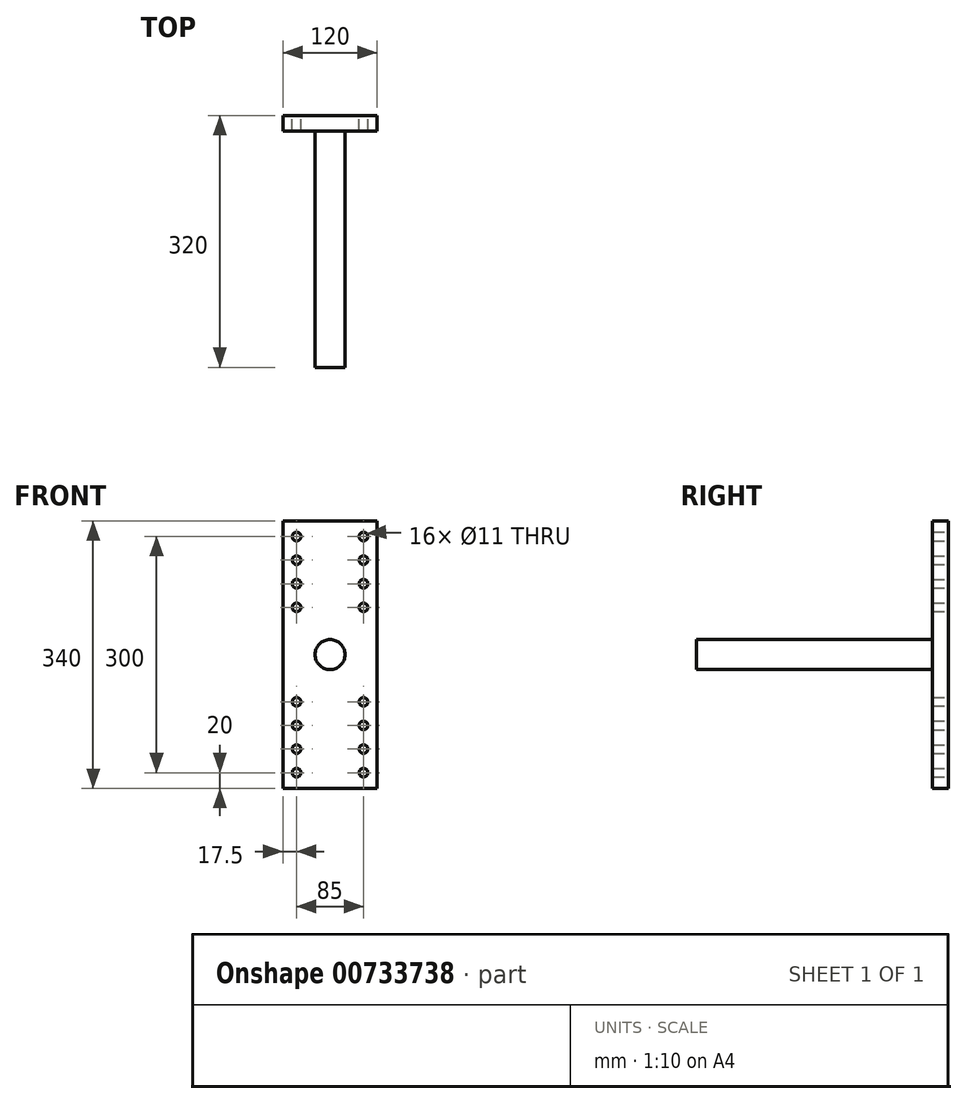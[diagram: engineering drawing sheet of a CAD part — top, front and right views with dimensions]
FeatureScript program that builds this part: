
annotation { "Feature Type Name" : "Feature", "Feature Type Description" : "" }
export const myFeature = defineFeature(function(context is Context, id is Id, definition is map)
    precondition{}
    {
        {
            var Q0;
            Q0=qCreatedBy(makeId("Front.planeOp"),FACE);
            var sketch = newSketch(context, id + "F0", { "sketchPlane" : qUnion([Q0])});
            skLineSegment(sketch, "E0.bottom", {"start": v(60, -170) * mm, "end": v(-60, -170) * mm});
            skLineSegment(sketch, "E0.top", {"start": v(60, 170) * mm, "end": v(-60, 170) * mm});
            skLineSegment(sketch, "E0.left", {"start": v(60, -170) * mm, "end": v(60, 170) * mm});
            skLineSegment(sketch, "E0.right", {"start": v(-60, -170) * mm, "end": v(-60, 170) * mm});
            skPoint(sketch, "E0.middle", {"position": v(0, 0) * mm});
            skLineSegment(sketch, "E1", {"start": v(0, 0) * mm, "end": v(42.5, 0) * mm, "construction": true});
            skPoint(sketch, "E1.endSnap0", {"position": v(60, 0) * mm});
            skCircle(sketch, "E2", {"center": v(42.5, 270) * mm, "radius": 5.5 * mm});
            skCircle(sketch, "E3.0.1.0", {"center": v(42.5, 240) * mm, "radius": 5.5 * mm});
            skCircle(sketch, "E3.0.2.0", {"center": v(42.5, 210) * mm, "radius": 5.5 * mm});
            skCircle(sketch, "E3.0.3.0", {"center": v(42.5, 180) * mm, "radius": 5.5 * mm});
            skCircle(sketch, "E3.0.4.0", {"center": v(42.5, 150) * mm, "radius": 5.5 * mm});
            skCircle(sketch, "E3.0.5.0", {"center": v(42.5, 120) * mm, "radius": 5.5 * mm});
            skLineSegment(sketch, "E3.direction1", {"start": v(42.5, 270) * mm, "end": v(67.5, 270) * mm, "construction": true});
            skLineSegment(sketch, "E3.direction2", {"start": v(42.5, 270) * mm, "end": v(42.5, 240) * mm, "construction": true});
            skCircle(sketch, "E4.0.0.6", {"center": v(42.5, 90) * mm, "radius": 5.5 * mm});
            skCircle(sketch, "E4.0.0.7", {"center": v(42.5, 60) * mm, "radius": 5.5 * mm});
            skCircle(sketch, "E5.MirrorC", {"center": v(42.5, -150) * mm, "radius": 5.5 * mm});
            skCircle(sketch, "E6.MirrorC", {"center": v(42.5, -270) * mm, "radius": 5.5 * mm});
            skCircle(sketch, "E7.MirrorC", {"center": v(42.5, -240) * mm, "radius": 5.5 * mm});
            skCircle(sketch, "E8.MirrorC", {"center": v(42.5, -210) * mm, "radius": 5.5 * mm});
            skCircle(sketch, "E9.MirrorC", {"center": v(42.5, -180) * mm, "radius": 5.5 * mm});
            skCircle(sketch, "E10.MirrorC", {"center": v(42.5, -120) * mm, "radius": 5.5 * mm});
            skCircle(sketch, "E11.MirrorC", {"center": v(42.5, -90) * mm, "radius": 5.5 * mm});
            skLineSegment(sketch, "E12.MirrorCS", {"start": v(42.5, -270) * mm, "end": v(42.5, -240) * mm, "construction": true});
            skCircle(sketch, "E13.MirrorC", {"center": v(42.5, -60) * mm, "radius": 5.5 * mm});
            skLineSegment(sketch, "E14.MirrorCS", {"start": v(42.5, -270) * mm, "end": v(67.5, -270) * mm, "construction": true});
            skLineSegment(sketch, "E15", {"start": v(0, 0) * mm, "end": v(0, 50) * mm, "construction": true});
            skCircle(sketch, "E16.MirrorC", {"center": v(-42.5, -240) * mm, "radius": 5.5 * mm});
            skCircle(sketch, "E17.MirrorC", {"center": v(-42.5, 90) * mm, "radius": 5.5 * mm});
            skLineSegment(sketch, "E18.MirrorCS", {"start": v(-42.5, 270) * mm, "end": v(-42.5, 240) * mm, "construction": true});
            skCircle(sketch, "E19.MirrorC", {"center": v(-42.5, 120) * mm, "radius": 5.5 * mm});
            skCircle(sketch, "E20.MirrorC", {"center": v(-42.5, -210) * mm, "radius": 5.5 * mm});
            skCircle(sketch, "E21.MirrorC", {"center": v(-42.5, 150) * mm, "radius": 5.5 * mm});
            skCircle(sketch, "E22.MirrorC", {"center": v(-42.5, -150) * mm, "radius": 5.5 * mm});
            skCircle(sketch, "E23.MirrorC", {"center": v(-42.5, 210) * mm, "radius": 5.5 * mm});
            skCircle(sketch, "E24.MirrorC", {"center": v(-42.5, 60) * mm, "radius": 5.5 * mm});
            skCircle(sketch, "E25.MirrorC", {"center": v(-42.5, -180) * mm, "radius": 5.5 * mm});
            skCircle(sketch, "E26.MirrorC", {"center": v(-42.5, -120) * mm, "radius": 5.5 * mm});
            skLineSegment(sketch, "E27.MirrorCS", {"start": v(-42.5, -270) * mm, "end": v(-42.5, -240) * mm, "construction": true});
            skCircle(sketch, "E28.MirrorC", {"center": v(-42.5, 180) * mm, "radius": 5.5 * mm});
            skCircle(sketch, "E29.MirrorC", {"center": v(-42.5, 240) * mm, "radius": 5.5 * mm});
            skCircle(sketch, "E30.MirrorC", {"center": v(-42.5, -270) * mm, "radius": 5.5 * mm});
            skCircle(sketch, "E31.MirrorC", {"center": v(-42.5, -60) * mm, "radius": 5.5 * mm});
            skCircle(sketch, "E32.MirrorC", {"center": v(-42.5, 270) * mm, "radius": 5.5 * mm});
            skCircle(sketch, "E33.MirrorC", {"center": v(-42.5, -90) * mm, "radius": 5.5 * mm});
            skSolve(sketch);
        }
        {
            var Q0;
            Q0=makeQuery(id+"F0.imprint","IMPRINT",FACE,{"disambiguationData":[TD([[makeQuery(id+"F0.imprint","IMPRINT",EDGE,{"derivedFrom":sQuery(id+"F0.wireOp",EDGE,"E0.bottom")}),-1.0]])]});
            extrude(context, id + "F1", {"entities" : qUnion([Q0]), "depth" : 20 * mm, "offsetDistance" : 25 * mm});
        }
        {
            var Q0;
            Q0=makeQuery(id+"F1.opExtrude","CAP_FACE",FACE,{"disambiguationData":[OSD([sQuery(id+"F0.wireOp",EDGE,"E0.bottom"),sQuery(id+"F0.wireOp",EDGE,"E0.top"),sQuery(id+"F0.wireOp",EDGE,"E0.left"),sQuery(id+"F0.wireOp",EDGE,"E0.right")])],"isStart":false});
            var sketch = newSketch(context, id + "F2", { "sketchPlane" : qUnion([Q0])});
            skCircle(sketch, "E34", {"center": v(0, 0) * mm, "radius": 19.05 * mm});
            skSolve(sketch);
        }
        {
            var Q0;
            Q0=makeQuery(id+"F2.imprint","IMPRINT",FACE,{"disambiguationData":[TD([[makeQuery(id+"F2.imprint","IMPRINT",EDGE,{"derivedFrom":sQuery(id+"F2.wireOp",EDGE,"E34")}),1.0]])]});
            extrude(context, id + "F3", {"entities" : qUnion([Q0]), "operationType" : NewBodyOperationType.ADD, "depth" : 300 * mm, "offsetDistance" : 25 * mm});
        }
    });
